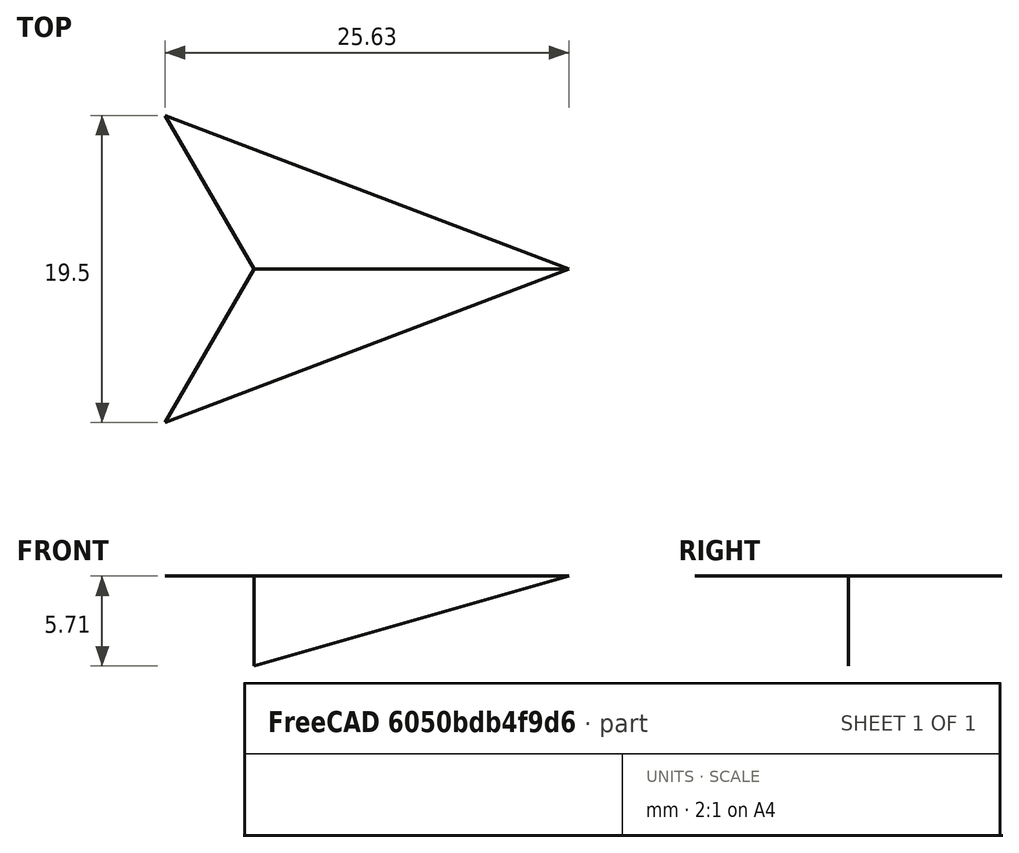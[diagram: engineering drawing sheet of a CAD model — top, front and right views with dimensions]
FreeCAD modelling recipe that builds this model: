
FCSTD DOCUMENT  (FreeCAD 0.21R32457 (Git))
Label: board outline
License: All rights reserved
LicenseURL: http://en.wikipedia.org/wiki/All_rights_reserved
objects: Part::FeaturePython×4, Sketcher::SketchObject×2, Part::Compound×1
note: 7 computed .brp shape members not serialized (recipe doc carries the construction recipe); baked Part::Feature solids carry a one-line shape summary decoded from their .brp

FEATURE [Sketcher::SketchObject] Sketch
  FullyConstrained = true
  sketch-geometry (4):
    g0: LineSegment StartX=18.58 StartY=-24.46 StartZ=0 EndX=134.58 EndY=-24.46 EndZ=0
    g1: LineSegment StartX=134.58 StartY=-24.46 StartZ=0 EndX=134.58 EndY=-106.46 EndZ=0
    g2: LineSegment StartX=134.58 StartY=-106.46 StartZ=0 EndX=18.58 EndY=-106.46 EndZ=0
    g3: LineSegment StartX=18.58 StartY=-106.46 StartZ=0 EndX=18.58 EndY=-24.46 EndZ=0
  constraints (12):
    c: Coincident(g0,g1)
    c: Coincident(g1,g2)
    c: Coincident(g2,g3)
    c: Coincident(g3,g0)
    c: Horizontal(g0)
    c: Horizontal(g2)
    c: Vertical(g1)
    c: Vertical(g3)
    c: DistanceX(g0) = 18.58
    c: DistanceY(g0) = -24.46
    c: DistanceX(g0,g0) = 116
    c: DistanceY(g1,g1) = 82
FEATURE [Part::FeaturePython] ArrayFromShape  label="Array from Sketch"  # WARN: FeaturePython — macro-defined, semantics opaque (R4)
  CompoundTraversal = 1
  ExposePlacement = false
  MarkerShape = 1
  MarkerSize = 20
  NumElements = 1
  OrientElementIndex = 0
  OrientMode = 1
  ShapeLink = -> Sketch
  TranslateElementIndex = 0
  TranslateMode = 4
  Type = lattice2ArrayFromShape.LatticeArrayFromShape
  isLattice = 1
FEATURE [Sketcher::SketchObject] Sketch001
  ExternalGeometry = -> [ArrayFromShape,Sketch]
  FullyConstrained = true
  sketch-geometry (6):
    g0: LineSegment StartX=76.58 StartY=-24.46 StartZ=0 EndX=138.08 EndY=-24.46 EndZ=0
    g1: ArcOfCircle CenterX=138.08 CenterY=-27.96 CenterZ=0 NormalX=0 NormalY=0 NormalZ=1 AngleXU=0 Radius=3.5 StartAngle=5.21473 EndAngle=7.85398
    g2: ArcOfCircle CenterX=144.58 CenterY=-39.7922 CenterZ=0 NormalX=0 NormalY=0 NormalZ=1 AngleXU=0 Radius=10 StartAngle=2.07314 EndAngle=3.14159
    g3: LineSegment StartX=134.58 StartY=-39.7922 StartZ=0 EndX=134.58 EndY=-65.46 EndZ=0
    g4: Circle CenterX=138.08 CenterY=-27.96 CenterZ=0 NormalX=0 NormalY=0 NormalZ=1 AngleXU=0 Radius=1.5
    g5: LineSegment StartX=134.58 StartY=-27.96 StartZ=0 EndX=136.58 EndY=-27.96 EndZ=0
  constraints (17):
    c: Tangent(g0,g1) = 1.5708
    c: Tangent(g1,g2) = 1.5708
    c: Tangent(g2,g3) = -1.5708
    c: Coincident(g4,g1)
    c: Vertical(g-3,g0)
    c: Horizontal(g3,g-3)
    c: PointOnObject(g0,g-4)
    c: Horizontal(g0)
    c: Vertical(g3)
    c: PointOnObject(g3,g-5)
    c: Diameter(g4) = 3
    c: Perpendicular(g5,g4) = 4.71239
    c: Perpendicular(g5,g-5) = 4.71239
    c: DistanceX(g5,g5) = 2
    c: Tangent(g1,g-5)
    c: DistanceX(g-3,g1) = 61.5
    c: Radius(g2) = 10
FEATURE [Part::FeaturePython] Mirror  label="Mirror of Sketch001"  # WARN: FeaturePython — macro-defined, semantics opaque (R4)
  ExposePlacement = false
  FlipX = false
  FlipY = true
  FlipZ = false
  MarkerShape = 1
  MarkerSize = 0
  NumElements = 0
  Object = -> Sketch001
  ObjectTraversal = 0
  Pivot = -> ArrayFromShape [Face1]
  PivotPlacement = pos=(76.58,-65.46,0) rot=(0,0,1;0rad)
  Type = lattice2Mirror.LatticeMirror
  isLattice = 0
FEATURE [Part::FeaturePython] Mirror001  label="Mirror001 of Sketch001"  # WARN: FeaturePython — macro-defined, semantics opaque (R4)
  ExposePlacement = false
  FlipX = true
  FlipY = true
  FlipZ = false
  MarkerShape = 1
  MarkerSize = 0
  NumElements = 0
  Object = -> Sketch001
  ObjectTraversal = 0
  Pivot = -> ArrayFromShape [Face1]
  PivotPlacement = pos=(76.58,-65.46,0) rot=(0,0,1;0rad)
  Type = lattice2Mirror.LatticeMirror
  isLattice = 0
FEATURE [Part::FeaturePython] Mirror002  label="Mirror002 of Sketch001"  # WARN: FeaturePython — macro-defined, semantics opaque (R4)
  ExposePlacement = false
  FlipX = true
  FlipY = false
  FlipZ = false
  MarkerShape = 1
  MarkerSize = 0
  NumElements = 0
  Object = -> Sketch001
  ObjectTraversal = 0
  Pivot = -> ArrayFromShape [Face1]
  PivotPlacement = pos=(76.58,-65.46,0) rot=(0,0,1;0rad)
  Type = lattice2Mirror.LatticeMirror
  isLattice = 0
FEATURE [Part::Compound] Compound
  Links = -> [Sketch001,Mirror,Mirror001,Mirror002]
